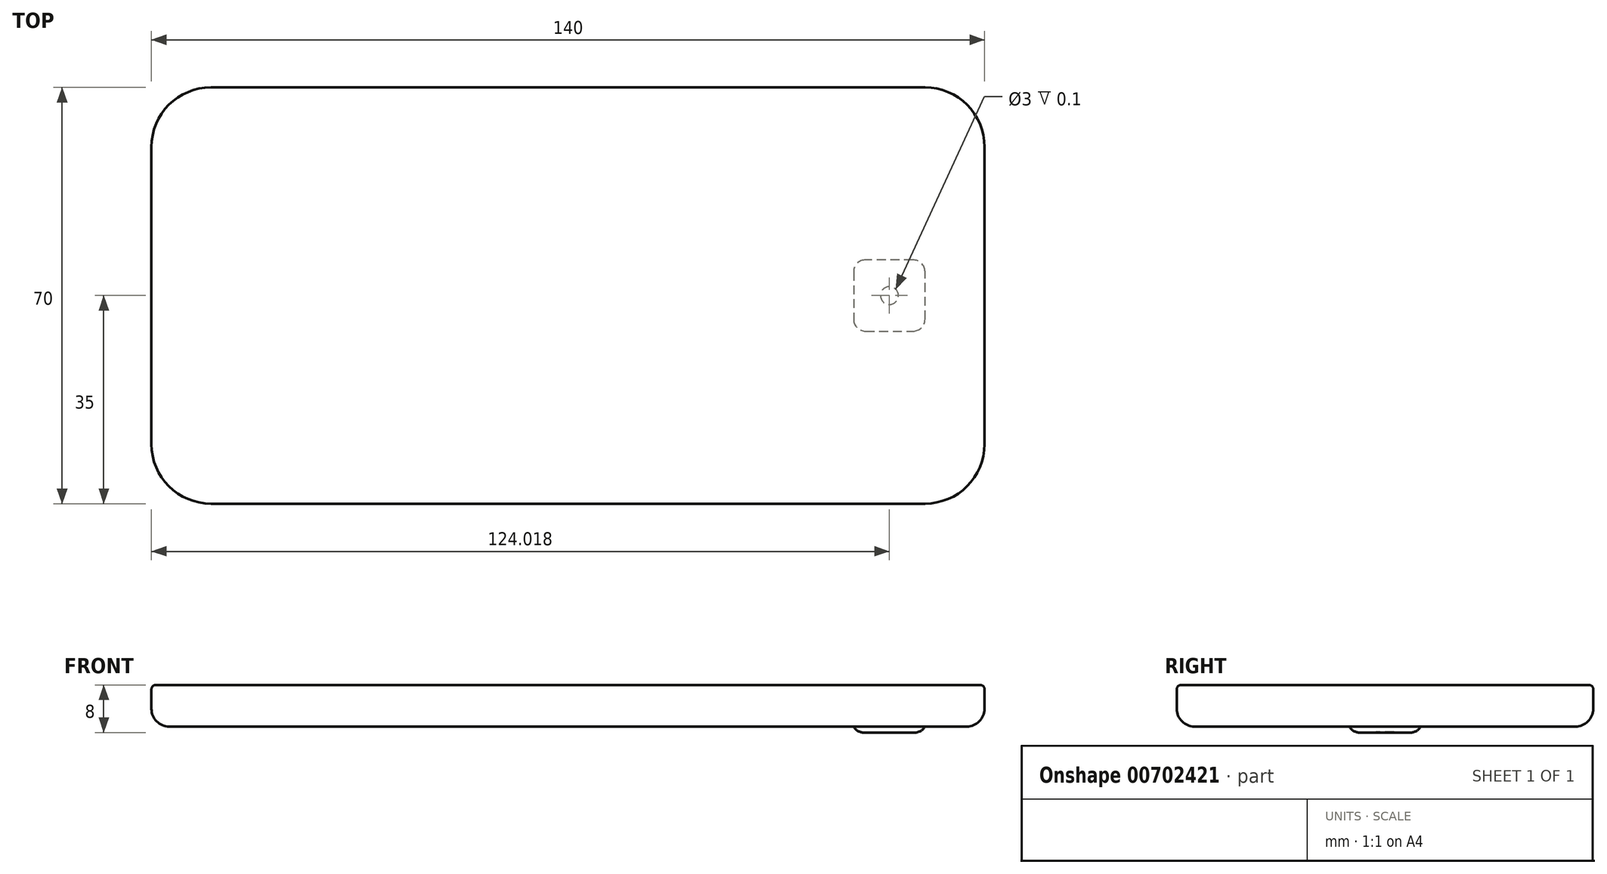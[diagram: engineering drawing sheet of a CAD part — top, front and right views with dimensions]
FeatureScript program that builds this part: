
annotation { "Feature Type Name" : "Feature", "Feature Type Description" : "" }
export const myFeature = defineFeature(function(context is Context, id is Id, definition is map)
    precondition{}
    {
        {
            var Q0;
            Q0=qCreatedBy(makeId("Top.planeOp"),FACE);
            var sketch = newSketch(context, id + "F0", { "sketchPlane" : qUnion([Q0])});
            skLineSegment(sketch, "E0", {"start": v(-51.4, 70) * mm, "end": v(-51.4, 0) * mm});
            skLineSegment(sketch, "E1", {"start": v(-51.4, 0) * mm, "end": v(88.6, 0) * mm});
            skLineSegment(sketch, "E2", {"start": v(88.6, 0) * mm, "end": v(88.6, 70) * mm});
            skLineSegment(sketch, "E3", {"start": v(88.6, 70) * mm, "end": v(-51.4, 70) * mm});
            skSolve(sketch);
        }
        {
            var Q0;
            Q0=makeQuery(id+"F0.imprint","IMPRINT",FACE,{"disambiguationData":[TD([[makeQuery(id+"F0.imprint","IMPRINT",EDGE,{"derivedFrom":sQuery(id+"F0.wireOp",EDGE,"E0")}),1.0]])]});
            extrude(context, id + "F1", {"entities" : qUnion([Q0]), "depth" : 7 * mm, "offsetDistance" : 25 * mm});
        }
        {
            var Q0;
            Q0=makeQuery(id+"F1.opExtrude","SWEPT_EDGE",EDGE,{"disambiguationData":[OSD([sQuery(id+"F0.wireOp",EDGE,"E2"),sQuery(id+"F0.wireOp",EDGE,"E3")])]});
            var Q1;
            Q1=makeQuery(id+"F1.opExtrude","SWEPT_EDGE",EDGE,{"disambiguationData":[OSD([sQuery(id+"F0.wireOp",EDGE,"E1"),sQuery(id+"F0.wireOp",EDGE,"E2")])]});
            var Q2;
            Q2=makeQuery(id+"F1.opExtrude","SWEPT_EDGE",EDGE,{"disambiguationData":[OSD([sQuery(id+"F0.wireOp",EDGE,"E0"),sQuery(id+"F0.wireOp",EDGE,"E1")])]});
            var Q3;
            Q3=makeQuery(id+"F1.opExtrude","SWEPT_EDGE",EDGE,{"disambiguationData":[OSD([sQuery(id+"F0.wireOp",EDGE,"E0"),sQuery(id+"F0.wireOp",EDGE,"E3")])]});
            fillet(context, id + "F2", {"entities" : qUnion([Q0, Q1, Q2, Q3]), "radius" : 10 * mm, "tangentPropagation" : true, "allowEdgeOverflow" : false});
        }
        {
            var Q0;
            Q0=makeQuery(id+"F1.opExtrude","CAP_EDGE",EDGE,{"disambiguationData":[OSD([sQuery(id+"F0.wireOp",EDGE,"E1")])],"isStart":false});
            fillet(context, id + "F3", {"entities" : qUnion([Q0]), "radius" : 0.7 * mm, "tangentPropagation" : true, "allowEdgeOverflow" : false});
        }
        {
            var Q0;
            Q0=makeQuery(id+"F1.opExtrude","CAP_EDGE",EDGE,{"disambiguationData":[OSD([sQuery(id+"F0.wireOp",EDGE,"E1")])],"isStart":true});
            fillet(context, id + "F4", {"entities" : qUnion([Q0]), "radius" : 3 * mm, "tangentPropagation" : true, "allowEdgeOverflow" : false});
        }
        {
            var Q0;
            Q0=makeQuery(id+"F1.opExtrude","CAP_FACE",FACE,{"disambiguationData":[OSD([sQuery(id+"F0.wireOp",EDGE,"E0"),sQuery(id+"F0.wireOp",EDGE,"E1"),sQuery(id+"F0.wireOp",EDGE,"E2"),sQuery(id+"F0.wireOp",EDGE,"E3")])],"isStart":true});
            var sketch = newSketch(context, id + "F5", { "sketchPlane" : qUnion([Q0])});
            skLineSegment(sketch, "E4", {"start": v(78.6, -35) * mm, "end": v(78.6, -41) * mm});
            skPoint(sketch, "E4.startSnap0", {"position": v(85.6, -35) * mm});
            skLineSegment(sketch, "E5", {"start": v(78.6, -41) * mm, "end": v(66.6, -41) * mm});
            skLineSegment(sketch, "E6", {"start": v(66.6, -41) * mm, "end": v(66.6, -29) * mm});
            skLineSegment(sketch, "E7", {"start": v(66.6, -29) * mm, "end": v(78.6, -29) * mm});
            skLineSegment(sketch, "E8", {"start": v(78.6, -29) * mm, "end": v(78.6, -35) * mm});
            skSolve(sketch);
        }
        {
            var Q0;
            Q0=makeQuery(id+"F5.imprint","IMPRINT",FACE,{"disambiguationData":[TD([[makeQuery(id+"F5.imprint","IMPRINT",EDGE,{"derivedFrom":sQuery(id+"F5.wireOp",EDGE,"E4")}),-1.0]])]});
            extrude(context, id + "F6", {"entities" : qUnion([Q0]), "operationType" : NewBodyOperationType.ADD, "depth" : 1 * mm, "offsetDistance" : 25 * mm});
        }
        {
            var Q0;
            Q0=makeQuery(id+"F6.opExtrude","SWEPT_EDGE",EDGE,{"disambiguationData":[OSD([sQuery(id+"F5.wireOp",EDGE,"E5"),sQuery(id+"F5.wireOp",EDGE,"E6")])]});
            var Q1;
            Q1=makeQuery(id+"F6.opExtrude","SWEPT_EDGE",EDGE,{"disambiguationData":[OSD([sQuery(id+"F5.wireOp",EDGE,"E6"),sQuery(id+"F5.wireOp",EDGE,"E7")])]});
            var Q2;
            Q2=makeQuery(id+"F6.opExtrude","SWEPT_EDGE",EDGE,{"disambiguationData":[OSD([sQuery(id+"F5.wireOp",EDGE,"E7"),sQuery(id+"F5.wireOp",EDGE,"E8")])]});
            var Q3;
            Q3=makeQuery(id+"F6.opExtrude","SWEPT_EDGE",EDGE,{"disambiguationData":[OSD([sQuery(id+"F5.wireOp",EDGE,"E4"),sQuery(id+"F5.wireOp",EDGE,"E5")])]});
            fillet(context, id + "F7", {"entities" : qUnion([Q0, Q1, Q2, Q3]), "radius" : 2 * mm, "tangentPropagation" : true, "allowEdgeOverflow" : false});
        }
        {
            var Q0;
            Q0=makeQuery(id+"F6.opExtrude","CAP_EDGE",EDGE,{"disambiguationData":[OSD([sQuery(id+"F5.wireOp",EDGE,"E5")])],"isStart":false});
            fillet(context, id + "F8", {"entities" : qUnion([Q0]), "radius" : 2 * mm, "tangentPropagation" : true, "allowEdgeOverflow" : false});
        }
        {
            var Q0;
            Q0=makeQuery(id+"F6.opExtrude","CAP_FACE",FACE,{"disambiguationData":[OSD([sQuery(id+"F5.wireOp",EDGE,"E4"),sQuery(id+"F5.wireOp",EDGE,"E5"),sQuery(id+"F5.wireOp",EDGE,"E6"),sQuery(id+"F5.wireOp",EDGE,"E7"),sQuery(id+"F5.wireOp",EDGE,"E8")])],"isStart":false});
            var Q1;
            Q1=makeQuery(id+"F1.opExtrude","CAP_FACE",FACE,{"disambiguationData":[OSD([sQuery(id+"F0.wireOp",EDGE,"E0"),sQuery(id+"F0.wireOp",EDGE,"E1"),sQuery(id+"F0.wireOp",EDGE,"E2"),sQuery(id+"F0.wireOp",EDGE,"E3")])],"isStart":true});
            extrude(context, id + "F9", {"entities" : qUnion([Q0, Q1]), "operationType" : NewBodyOperationType.REMOVE, "depth" : 0.5 * mm, "offsetDistance" : 25 * mm});
        }
        {
            var Q0;
            Q0=makeQuery(id+"F6.opExtrude","CAP_FACE",FACE,{"disambiguationData":[OSD([sQuery(id+"F5.wireOp",EDGE,"E4"),sQuery(id+"F5.wireOp",EDGE,"E5"),sQuery(id+"F5.wireOp",EDGE,"E6"),sQuery(id+"F5.wireOp",EDGE,"E7"),sQuery(id+"F5.wireOp",EDGE,"E8")])],"isStart":false});
            var sketch = newSketch(context, id + "F10", { "sketchPlane" : qUnion([Q0])});
            skCircle(sketch, "E9", {"center": v(72.63, -35) * mm, "radius": 1.5 * mm});
            skPoint(sketch, "E9.centerSnap0", {"position": v(68.34, -35) * mm});
            skSolve(sketch);
        }
        {
            var Q0;
            Q0=makeQuery(id+"F10.imprint","IMPRINT",FACE,{"disambiguationData":[TD([[makeQuery(id+"F10.imprint","IMPRINT",EDGE,{"derivedFrom":sQuery(id+"F10.wireOp",EDGE,"E9")}),1.0]])]});
            extrude(context, id + "F11", {"entities" : qUnion([Q0]), "operationType" : NewBodyOperationType.REMOVE, "oppositeDirection" : true, "depth" : 0.1 * mm, "offsetDistance" : 25 * mm});
        }
    });
